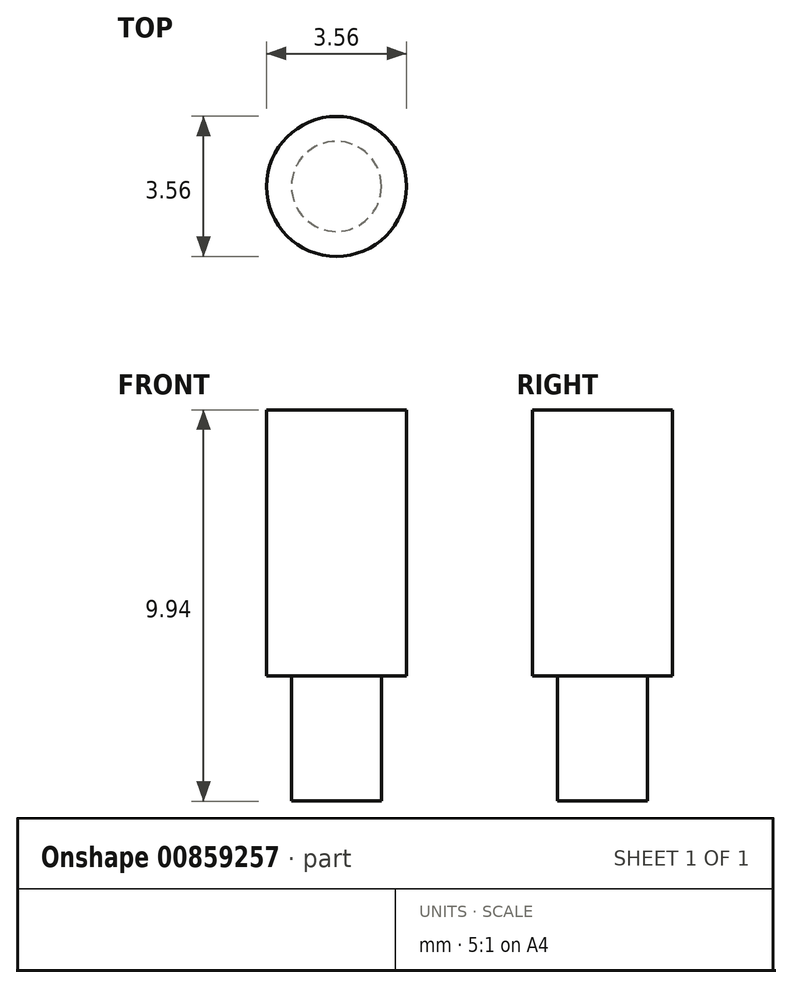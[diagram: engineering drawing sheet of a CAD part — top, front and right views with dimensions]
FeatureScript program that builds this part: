
annotation { "Feature Type Name" : "Feature", "Feature Type Description" : "" }
export const myFeature = defineFeature(function(context is Context, id is Id, definition is map)
    precondition{}
    {
        {
            var Q0;
            Q0=qCreatedBy(makeId("Top.planeOp"),FACE);
            var sketch = newSketch(context, id + "F0", { "sketchPlane" : qUnion([Q0])});
            skCircle(sketch, "E0", {"center": v(0, 0) * mm, "radius": 1.78 * mm});
            skSolve(sketch);
        }
        {
            var Q0;
            Q0 = qSketchRegion(id + "F0", true);
            extrude(context, id + "F1", {"entities" : qUnion([Q0]), "depth" : 6.76 * mm, "offsetDistance" : 25.4 * mm});
        }
        {
            var Q0;
            Q0=makeQuery(id+"F1.opExtrude","CAP_FACE",FACE,{"disambiguationData":[OSD([sQuery(id+"F0.wireOp",EDGE,"E0")])],"isStart":false});
            var sketch = newSketch(context, id + "F2", { "sketchPlane" : qUnion([Q0])});
            skSolve(sketch);
        }
        {
            var Q0;
            Q0=makeQuery(id+"F2.imprint","IMPRINT",FACE,{"disambiguationData":[TD([[makeQuery(id+"F2.imprint","IMPRINT",EDGE,{"derivedFrom":makeQuery(id+"F1.opExtrude","CAP_EDGE",EDGE,{"disambiguationData":[OSD([sQuery(id+"F0.wireOp",EDGE,"E0")])],"isStart":false})}),1.0]])]});
            var sketch = newSketch(context, id + "F3", { "sketchPlane" : qUnion([Q0])});
            skCircle(sketch, "E1", {"center": v(0, 0) * mm, "radius": 1.17 * mm});
            skSolve(sketch);
        }
        {
            var Q0;
            Q0 = qSketchRegion(id + "F3", true);
            extrude(context, id + "F4", {"entities" : qUnion([Q0]), "operationType" : NewBodyOperationType.REMOVE, "depth" : 3.17 * mm, "offsetDistance" : 25.4 * mm});
        }
        {
            var Q0;
            Q0=makeQuery(id+"F1.opExtrude","CAP_FACE",FACE,{"disambiguationData":[OSD([sQuery(id+"F0.wireOp",EDGE,"E0")])],"isStart":true});
            var sketch = newSketch(context, id + "F5", { "sketchPlane" : qUnion([Q0])});
            skCircle(sketch, "E2", {"center": v(0, 0) * mm, "radius": 1.14 * mm});
            skSolve(sketch);
        }
        {
            var Q0;
            Q0 = qSketchRegion(id + "F5", true);
            extrude(context, id + "F6", {"entities" : qUnion([Q0]), "operationType" : NewBodyOperationType.ADD, "depth" : 3.17 * mm, "offsetDistance" : 25.4 * mm});
        }
    });
